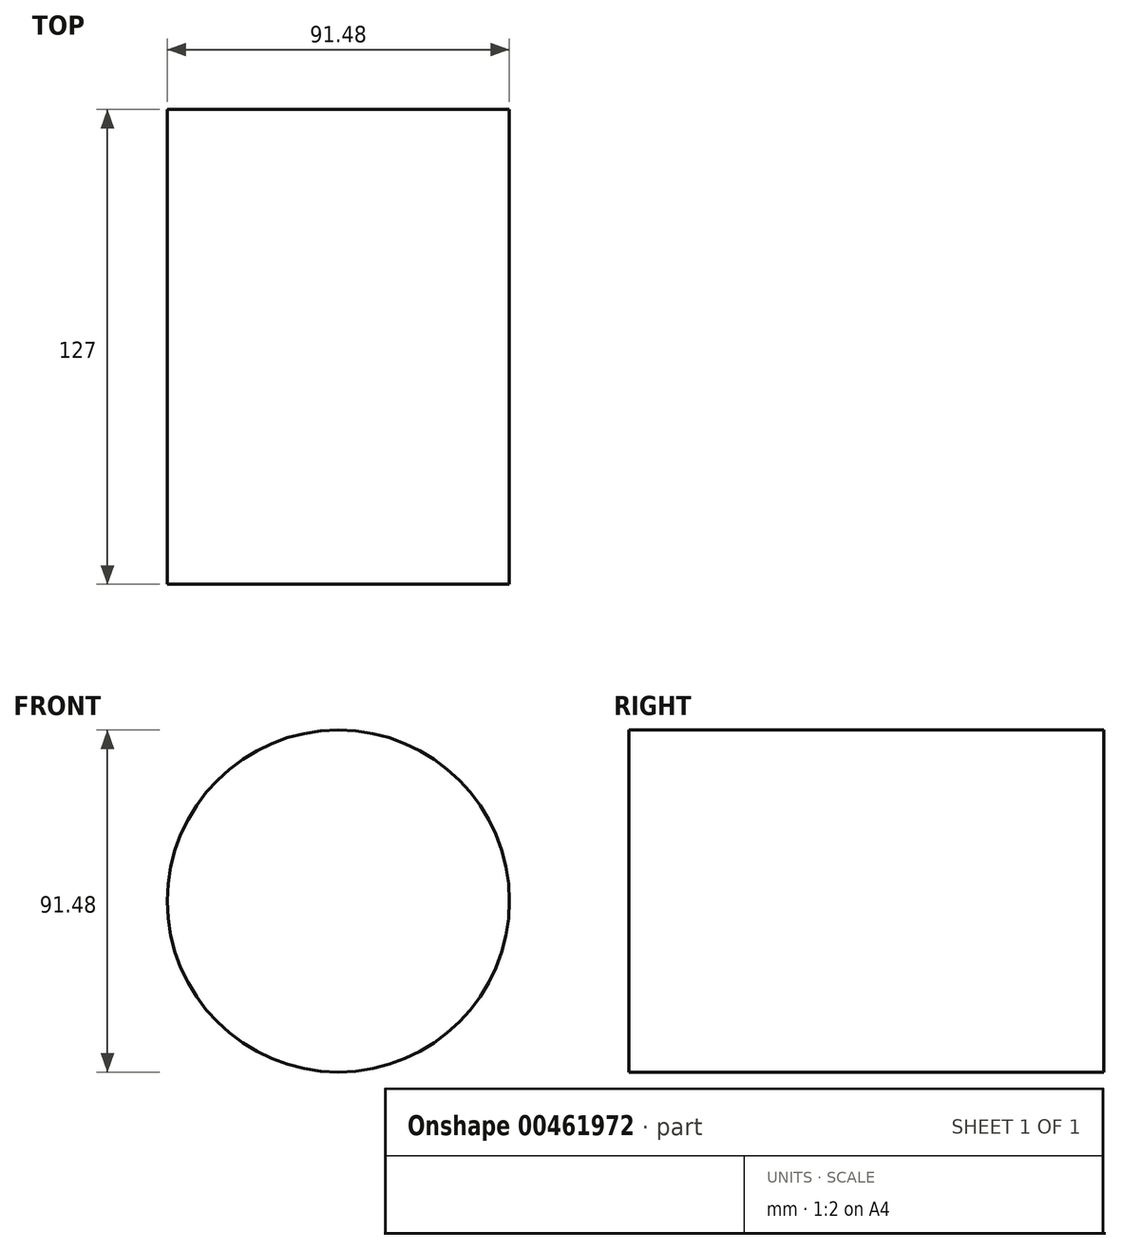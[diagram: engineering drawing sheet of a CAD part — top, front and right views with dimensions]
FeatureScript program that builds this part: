
annotation { "Feature Type Name" : "Feature", "Feature Type Description" : "" }
export const myFeature = defineFeature(function(context is Context, id is Id, definition is map)
    precondition{}
    {
        {
            var Q0;
            Q0=qCreatedBy(makeId("Front.planeOp"),FACE);
            var sketch = newSketch(context, id + "F0", { "sketchPlane" : qUnion([Q0])});
            skCircle(sketch, "E0", {"center": v(0, 0) * mm, "radius": 45.74 * mm});
            skSolve(sketch);
        }
        {
            var Q0;
            Q0 = qSketchRegion(id + "F0", true);
            extrude(context, id + "F1", {"entities" : qUnion([Q0]), "oppositeDirection" : true, "depth" : 127 * mm});
        }
    });
